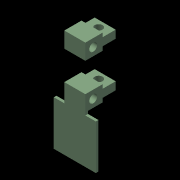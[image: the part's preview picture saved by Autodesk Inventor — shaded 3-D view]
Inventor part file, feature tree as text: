
AUTODESK INVENTOR PART (.ipt)
format: ipt  version: 2020 (Build 240168000, 168)  size: 203,264 bytes
history: native  units: mm
features: extrude x6, projected_geometry x5, thread x4, other x1, pattern_linear x1
ambient origin geometry x8: Origin, YZ Plane, XZ Plane, XY Plane, X Axis, Y Axis, Z Axis, Center Point
bodies: Body1 (feature_tree)
feature tree (17):
  other  "實體1"
  extrude  "Extrusion1"  Depth=3.0mm
  pattern_linear  "Rectangular Pattern1"  Spacing1=5.0mm  [1 undecoded]
  extrude  "Extrusion2"  Depth=3.0mm TaperAngle=0.0deg
  extrude  "Extrusion3"  Depth=20.0mm
  extrude  "Extrusion4"  Depth=6.05mm
  extrude  "Extrusion5"  Depth=3.0mm
  extrude  "Extrusion6"  Depth=3.0mm
  thread  "Thread1"  [1 undecoded]
  thread  "Thread2"  [1 undecoded]
  thread  "Thread3"  [1 undecoded]
  thread  "Thread4"  [1 undecoded]
  projected_geometry  "Projected Loop1"
  projected_geometry  "Projected Loop2"
  projected_geometry  "Projected Loop3"
  projected_geometry  "Projected Loop4"
  projected_geometry  "Projected Loop5"
note: 5 required parameter values undecoded (feature->parameter linkage not recoverable at this tier; creation-order binding heuristic only, values carry confidence <= 0.55)
